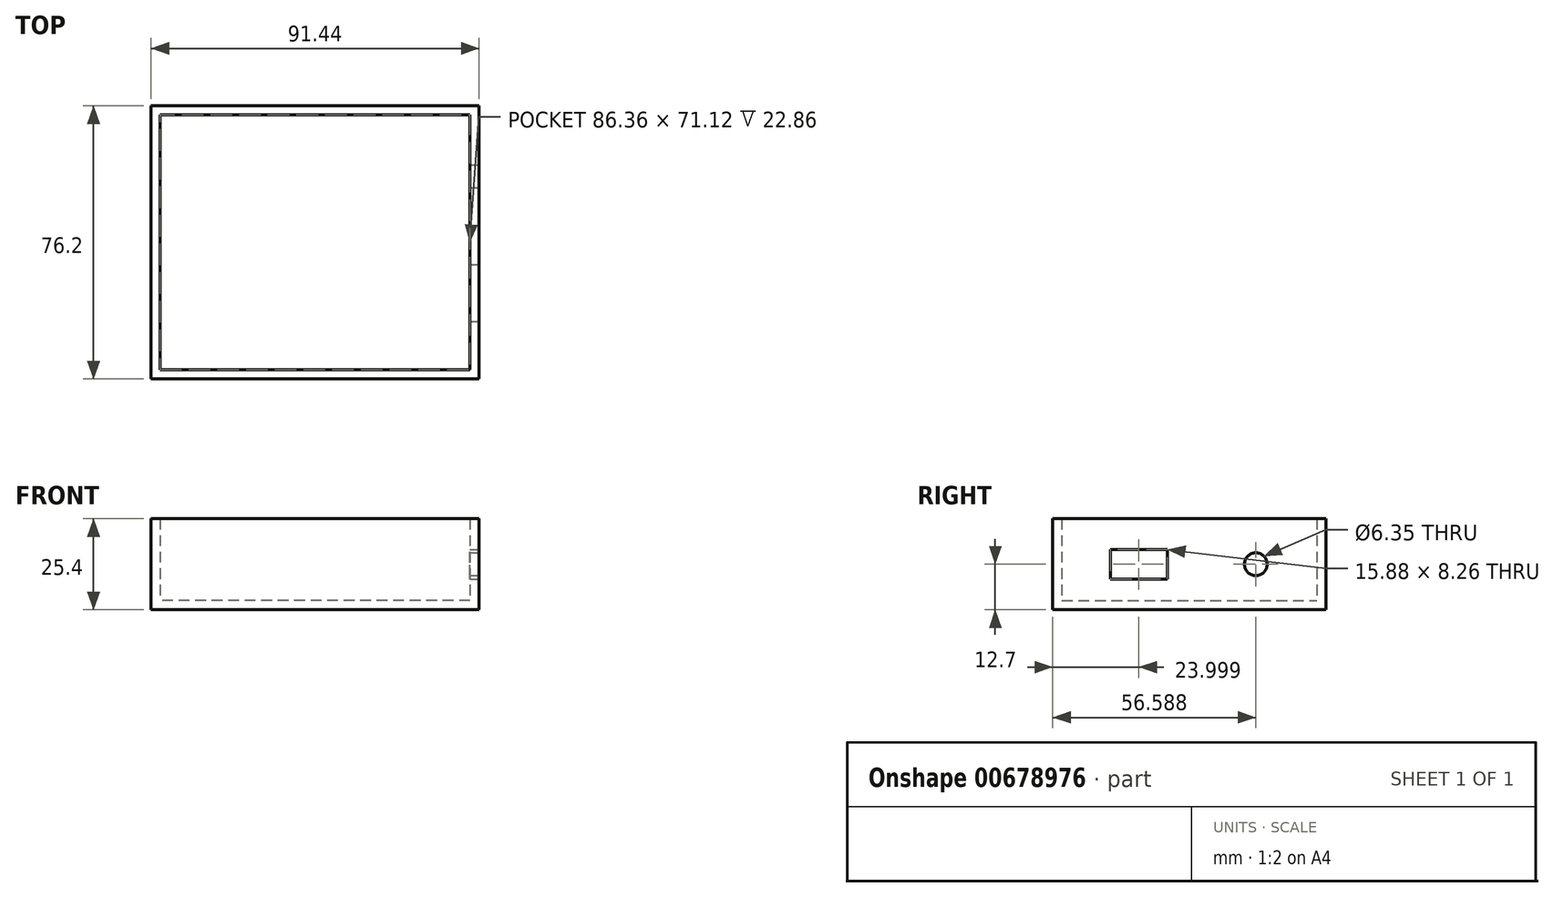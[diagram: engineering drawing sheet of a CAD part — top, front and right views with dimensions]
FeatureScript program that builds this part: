
annotation { "Feature Type Name" : "Feature", "Feature Type Description" : "" }
export const myFeature = defineFeature(function(context is Context, id is Id, definition is map)
    precondition{}
    {
        {
            var Q0;
            Q0=qCreatedBy(makeId("Front.planeOp"),FACE);
            var sketch = newSketch(context, id + "F0", { "sketchPlane" : qUnion([Q0])});
            skLineSegment(sketch, "E0.bottom", {"start": v(45.72, 12.7) * mm, "end": v(-45.72, 12.7) * mm});
            skLineSegment(sketch, "E0.top", {"start": v(45.72, -12.7) * mm, "end": v(-45.72, -12.7) * mm});
            skLineSegment(sketch, "E0.left", {"start": v(45.72, 12.7) * mm, "end": v(45.72, -12.7) * mm});
            skLineSegment(sketch, "E0.right", {"start": v(-45.72, 12.7) * mm, "end": v(-45.72, -12.7) * mm});
            skPoint(sketch, "E0.middle", {"position": v(0, 0) * mm});
            skSolve(sketch);
        }
        {
            var Q0;
            Q0=makeQuery(id+"F0.imprint","IMPRINT",FACE,{"disambiguationData":[TD([[makeQuery(id+"F0.imprint","IMPRINT",EDGE,{"derivedFrom":sQuery(id+"F0.wireOp",EDGE,"E0.bottom")}),1.0]])]});
            extrude(context, id + "F1", {"entities" : qUnion([Q0]), "endBound" : BoundingType.SYMMETRIC, "depth" : 76.2 * mm, "offsetDistance" : 25.4 * mm});
        }
        {
            var Q0;
            Q0=makeQuery(id+"F1.opExtrude","SWEPT_FACE",FACE,{"disambiguationData":[OSD([sQuery(id+"F0.wireOp",EDGE,"E0.bottom")])]});
            shell(context, id + "F2", {"entities" : qUnion([Q0]), "thickness" : 2.54 * mm});
        }
        {
            var Q0;
            Q0=makeQuery(id+"F1.opExtrude","SWEPT_FACE",FACE,{"disambiguationData":[OSD([sQuery(id+"F0.wireOp",EDGE,"E0.left")])]});
            var sketch = newSketch(context, id + "F3", { "sketchPlane" : qUnion([Q0])});
            skLineSegment(sketch, "E1.bottom", {"start": v(-6.16, 4.13) * mm, "end": v(-22.04, 4.13) * mm});
            skLineSegment(sketch, "E1.top", {"start": v(-6.16, -4.13) * mm, "end": v(-22.04, -4.13) * mm});
            skLineSegment(sketch, "E1.left", {"start": v(-6.16, 4.13) * mm, "end": v(-6.16, -4.13) * mm});
            skLineSegment(sketch, "E1.right", {"start": v(-22.04, 4.13) * mm, "end": v(-22.04, -4.13) * mm});
            skPoint(sketch, "E1.middle", {"position": v(-14.1, 0) * mm});
            skCircle(sketch, "E2", {"center": v(18.49, 0) * mm, "radius": 3.18 * mm});
            skSolve(sketch);
        }
        {
            var Q0;
            Q0=makeQuery(id+"F3.imprint","IMPRINT",FACE,{"disambiguationData":[TD([[makeQuery(id+"F3.imprint","IMPRINT",EDGE,{"derivedFrom":sQuery(id+"F3.wireOp",EDGE,"E1.bottom")}),1.0]])]});
            var Q1;
            Q1=makeQuery(id+"F3.imprint","IMPRINT",FACE,{"disambiguationData":[TD([[makeQuery(id+"F3.imprint","IMPRINT",EDGE,{"derivedFrom":sQuery(id+"F3.wireOp",EDGE,"E2")}),1.0]])]});
            extrude(context, id + "F4", {"entities" : qUnion([Q0, Q1]), "operationType" : NewBodyOperationType.REMOVE, "endBound" : BoundingType.UP_TO_NEXT, "oppositeDirection" : true, "depth" : 25.4 * mm, "offsetDistance" : 25.4 * mm});
        }
    });
